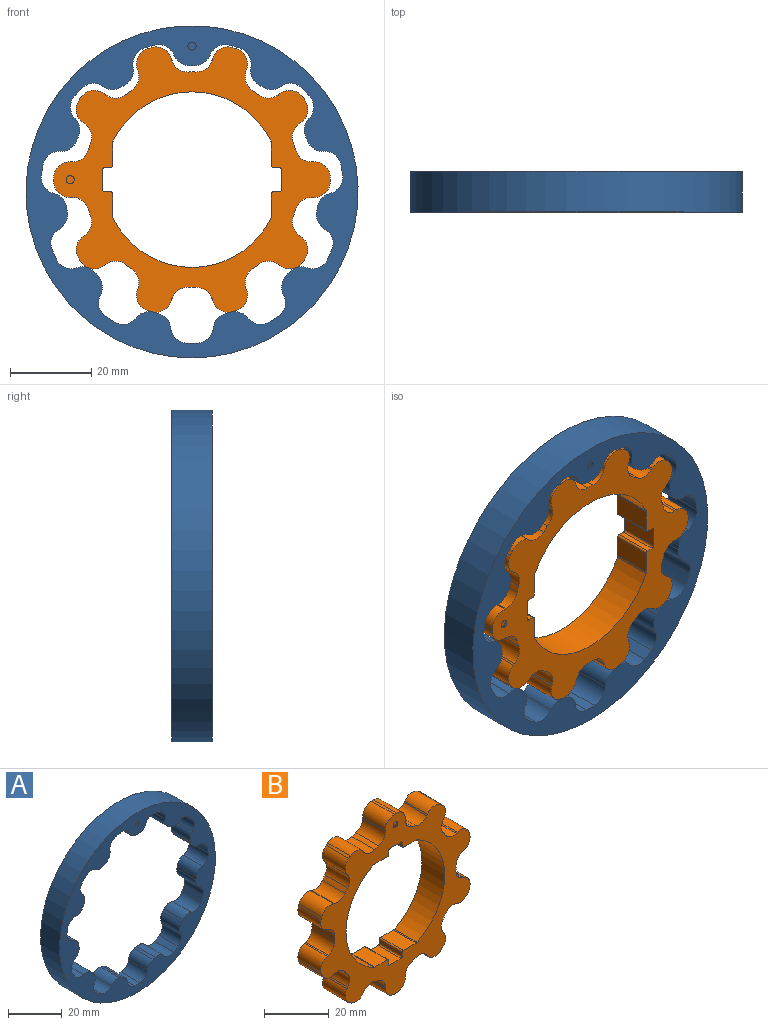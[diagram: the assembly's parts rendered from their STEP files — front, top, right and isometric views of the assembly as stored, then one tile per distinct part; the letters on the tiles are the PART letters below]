
ASSEMBLY  parts=2 mates=1
PART A: 71 faces, bbox 81.7x10x81.7 mm
  f0: cylinder r=31.07mm len=9.95mm, axis (0,1,0), area 12.2mm2, adj f11,f12,f18,f46
  f1: cylinder r=31.07mm len=9.95mm, axis (0,1,0), area 12.2mm2, adj f11,f12,f45,f48
  f2: cylinder r=31.07mm len=9.95mm, axis (0,1,0), area 12.2mm2, adj f11,f12,f42,f43
  f3: cylinder r=31.07mm len=9.95mm, axis (0,1,0), area 12.2mm2, adj f11,f12,f39,f40
  f4: cylinder r=31.07mm len=9.95mm, axis (0,1,0), area 12.2mm2, adj f11,f12,f36,f37
  f5: cylinder r=31.07mm len=9.95mm, axis (0,1,0), area 12.2mm2, adj f11,f12,f33,f34
  f6: cylinder r=31.07mm len=9.95mm, axis (0,1,0), area 12.2mm2, adj f11,f12,f30,f31
  f7: cylinder r=31.07mm len=9.95mm, axis (0,1,0), area 12.2mm2, adj f11,f12,f27,f28
  f8: cylinder r=31.07mm len=9.95mm, axis (0,1,0), area 12.2mm2, adj f11,f12,f24,f25
  f9: cylinder r=31.07mm len=9.95mm, axis (0,1,0), area 12.2mm2, adj f11,f12,f21,f22
  f10: cylinder r=31.07mm len=9.95mm, axis (0,1,0), area 12.2mm2, adj f11,f12,f17,f19
  f11: plane 81.72x81.72mm, normal (0,-1,0), area 1518mm2, adj f0,f1,f2,f3,f4,f5,f6,f7
  f12: plane 81.72x81.72mm, normal (0,1,0), area 1521.2mm2, adj f0,f1,f2,f3,f4,f5,f6,f7
  f13: cylinder r=40.86mm len=81.72mm, axis (0,1,0), area 2554.5mm2, adj f11,f12
  f14: cylinder r=1mm len=2mm, axis (0,-1,0), area 3.1mm2, adj f11,f15
  f15: plane 2x2mm, normal (0,-1,0), area 3.1mm2, adj f14
  f16: cylinder r=37.24mm len=9.95mm, axis (0,-1,0), area 27.6mm2, adj f11,f12,f69,f70
  f17: cylinder r=4mm len=9.95mm, axis (0,-1,0), area 48.8mm2, adj f10,f11,f12,f69
  f18: cylinder r=4mm len=9.95mm, axis (0,-1,0), area 48.8mm2, adj f0,f11,f12,f70
  f19: cylinder r=4mm len=9.95mm, axis (0,-1,0), area 48.8mm2, adj f10,f11,f12,f68
  f20: cylinder r=37.24mm len=9.95mm, axis (0,-1,0), area 27.6mm2, adj f11,f12,f67,f68
  f21: cylinder r=4mm len=9.95mm, axis (0,-1,0), area 48.8mm2, adj f9,f11,f12,f67
  f22: cylinder r=4mm len=9.95mm, axis (0,-1,0), area 48.8mm2, adj f9,f11,f12,f66
  f23: cylinder r=37.24mm len=9.95mm, axis (0,-1,0), area 27.6mm2, adj f11,f12,f65,f66
  f24: cylinder r=4mm len=9.95mm, axis (0,-1,0), area 48.8mm2, adj f8,f11,f12,f65
  f25: cylinder r=4mm len=9.95mm, axis (0,-1,0), area 48.8mm2, adj f8,f11,f12,f64
  f26: cylinder r=37.24mm len=9.95mm, axis (0,-1,0), area 27.6mm2, adj f11,f12,f63,f64
  f27: cylinder r=4mm len=9.95mm, axis (0,-1,0), area 48.8mm2, adj f7,f11,f12,f63
  f28: cylinder r=4mm len=9.95mm, axis (0,-1,0), area 48.8mm2, adj f7,f11,f12,f62
  f29: cylinder r=37.24mm len=9.95mm, axis (0,-1,0), area 27.6mm2, adj f11,f12,f61,f62
  f30: cylinder r=4mm len=9.95mm, axis (0,-1,0), area 48.8mm2, adj f6,f11,f12,f61
  f31: cylinder r=4mm len=9.95mm, axis (0,-1,0), area 48.8mm2, adj f6,f11,f12,f60
  f32: cylinder r=37.24mm len=9.95mm, axis (0,-1,0), area 27.6mm2, adj f11,f12,f59,f60
  f33: cylinder r=4mm len=9.95mm, axis (0,-1,0), area 48.8mm2, adj f5,f11,f12,f59
  f34: cylinder r=4mm len=9.95mm, axis (0,-1,0), area 48.8mm2, adj f5,f11,f12,f58
  f35: cylinder r=37.24mm len=9.95mm, axis (0,-1,0), area 27.6mm2, adj f11,f12,f57,f58
  f36: cylinder r=4mm len=9.95mm, axis (0,-1,0), area 48.8mm2, adj f4,f11,f12,f57
  f37: cylinder r=4mm len=9.95mm, axis (0,-1,0), area 48.8mm2, adj f4,f11,f12,f56
  f38: cylinder r=37.24mm len=9.95mm, axis (0,-1,0), area 27.6mm2, adj f11,f12,f55,f56
  f39: cylinder r=4mm len=9.95mm, axis (0,-1,0), area 48.8mm2, adj f3,f11,f12,f55
  f40: cylinder r=4mm len=9.95mm, axis (0,-1,0), area 48.8mm2, adj f3,f11,f12,f54
  f41: cylinder r=37.24mm len=9.95mm, axis (0,-1,0), area 27.6mm2, adj f11,f12,f53,f54
  f42: cylinder r=4mm len=9.95mm, axis (0,-1,0), area 48.8mm2, adj f2,f11,f12,f53
  f43: cylinder r=4mm len=9.95mm, axis (0,-1,0), area 48.8mm2, adj f2,f11,f12,f52
  f44: cylinder r=37.24mm len=9.95mm, axis (0,-1,0), area 27.6mm2, adj f11,f12,f51,f52
  f45: cylinder r=4mm len=9.95mm, axis (0,-1,0), area 48.8mm2, adj f1,f11,f12,f51
  f46: cylinder r=4mm len=9.95mm, axis (0,-1,0), area 48.8mm2, adj f0,f11,f12,f49
  f47: cylinder r=37.24mm len=9.95mm, axis (0,-1,0), area 27.6mm2, adj f11,f12,f49,f50
  f48: cylinder r=4mm len=9.95mm, axis (0,-1,0), area 48.8mm2, adj f1,f11,f12,f50
  f49: cylinder r=4mm len=9.95mm, axis (0,-1,0), area 57.9mm2, adj f11,f12,f46,f47
  f50: cylinder r=4mm len=9.95mm, axis (0,-1,0), area 57.9mm2, adj f11,f12,f47,f48
  f51: cylinder r=4mm len=9.95mm, axis (0,-1,0), area 57.9mm2, adj f11,f12,f44,f45
  f52: cylinder r=4mm len=9.95mm, axis (0,-1,0), area 57.9mm2, adj f11,f12,f43,f44
  f53: cylinder r=4mm len=9.95mm, axis (0,-1,0), area 57.9mm2, adj f11,f12,f41,f42
  f54: cylinder r=4mm len=9.95mm, axis (0,-1,0), area 57.9mm2, adj f11,f12,f40,f41
  f55: cylinder r=4mm len=9.95mm, axis (0,-1,0), area 57.9mm2, adj f11,f12,f38,f39
  f56: cylinder r=4mm len=9.95mm, axis (0,-1,0), area 57.9mm2, adj f11,f12,f37,f38
  f57: cylinder r=4mm len=9.95mm, axis (0,-1,0), area 57.9mm2, adj f11,f12,f35,f36
  f58: cylinder r=4mm len=9.95mm, axis (0,-1,0), area 57.9mm2, adj f11,f12,f34,f35
  f59: cylinder r=4mm len=9.95mm, axis (0,-1,0), area 57.9mm2, adj f11,f12,f32,f33
  f60: cylinder r=4mm len=9.95mm, axis (0,-1,0), area 57.9mm2, adj f11,f12,f31,f32
  f61: cylinder r=4mm len=9.95mm, axis (0,-1,0), area 57.9mm2, adj f11,f12,f29,f30
  f62: cylinder r=4mm len=9.95mm, axis (0,-1,0), area 57.9mm2, adj f11,f12,f28,f29
  f63: cylinder r=4mm len=9.95mm, axis (0,-1,0), area 57.9mm2, adj f11,f12,f26,f27
  f64: cylinder r=4mm len=9.95mm, axis (0,-1,0), area 57.9mm2, adj f11,f12,f25,f26
  f65: cylinder r=4mm len=9.95mm, axis (0,-1,0), area 57.9mm2, adj f11,f12,f23,f24
  f66: cylinder r=4mm len=9.95mm, axis (0,-1,0), area 57.9mm2, adj f11,f12,f22,f23
  f67: cylinder r=4mm len=9.95mm, axis (0,-1,0), area 57.9mm2, adj f11,f12,f20,f21
  f68: cylinder r=4mm len=9.95mm, axis (0,-1,0), area 57.9mm2, adj f11,f12,f19,f20
  f69: cylinder r=4mm len=9.95mm, axis (0,-1,0), area 57.9mm2, adj f11,f12,f16,f17
  f70: cylinder r=4mm len=9.95mm, axis (0,-1,0), area 57.9mm2, adj f11,f12,f16,f18
PART B: 108 faces, bbox 65.3x10x68 mm
  f0: cylinder r=34mm len=9.95mm, axis (0,1,0), area 9.4mm2, adj f9,f10,f41,f101
  f1: cylinder r=34mm len=9.95mm, axis (0,1,0), area 9.4mm2, adj f9,f10,f100,f107
  f2: cylinder r=34mm len=9.95mm, axis (0,1,0), area 9.4mm2, adj f9,f10,f93,f94
  f3: cylinder r=34mm len=9.95mm, axis (0,1,0), area 9.4mm2, adj f9,f10,f86,f87
  f4: cylinder r=34mm len=9.95mm, axis (0,1,0), area 9.4mm2, adj f9,f10,f79,f80
  f5: cylinder r=34mm len=9.95mm, axis (0,1,0), area 9.4mm2, adj f9,f10,f72,f73
  f6: cylinder r=34mm len=9.95mm, axis (0,1,0), area 9.4mm2, adj f9,f10,f65,f66
  f7: cylinder r=34mm len=9.95mm, axis (0,1,0), area 9.4mm2, adj f9,f10,f58,f59
  f8: cylinder r=34mm len=9.95mm, axis (0,1,0), area 9.4mm2, adj f9,f10,f51,f52
  f9: plane 68x65.32mm, normal (0,-1,0), area 1401.2mm2, adj f0,f1,f2,f3,f4,f5,f6,f7
  f10: plane 68x65.32mm, normal (0,1,0), area 1404.3mm2, adj f0,f1,f2,f3,f4,f5,f6,f7
  f11: cylinder r=1mm len=9.95mm, axis (0,1,0), area 4.5mm2, adj f9,f10,f12,f34
  f12: plane 9.95x5.56mm, normal (0,0,-1), area 55.3mm2, adj f9,f10,f11,f13
  f13: cylinder r=0.5mm len=9.95mm, axis (0,1,0), area 7.8mm2, adj f9,f10,f12,f14
  f14: plane 9.95x1.5mm, normal (1,0,0), area 14.9mm2, adj f9,f10,f13,f15
  f15: cylinder r=0.5mm len=9.95mm, axis (0,1,0), area 7.8mm2, adj f9,f10,f14,f16
  f16: plane 9.95x5mm, normal (0,0,-1), area 49.8mm2, adj f9,f10,f15,f17
  f17: cylinder r=0.5mm len=9.95mm, axis (0,1,0), area 7.8mm2, adj f9,f10,f16,f18
  f18: plane 9.95x1.5mm, normal (-1,0,0), area 14.9mm2, adj f9,f10,f17,f19
  f19: cylinder r=0.5mm len=9.95mm, axis (0,1,0), area 7.8mm2, adj f9,f10,f18,f20
  f20: plane 9.95x5.56mm, normal (0,0,-1), area 55.3mm2, adj f9,f10,f19,f21
  f21: cylinder r=1mm len=9.95mm, axis (0,1,0), area 4.5mm2, adj f9,f10,f20,f22
  f22: cylinder r=21.6mm len=38.8mm, axis (0,1,0), area 479.4mm2, adj f9,f10,f21,f23
  f23: cylinder r=1mm len=9.95mm, axis (0,1,0), area 4.5mm2, adj f9,f10,f22,f24
  f24: plane 9.95x5.56mm, normal (0,0,1), area 55.3mm2, adj f9,f10,f23,f25
  f25: cylinder r=0.5mm len=9.95mm, axis (0,1,0), area 7.8mm2, adj f9,f10,f24,f26
  f26: plane 9.95x1.5mm, normal (-1,0,0), area 14.9mm2, adj f9,f10,f25,f27
  f27: cylinder r=0.5mm len=9.95mm, axis (0,1,0), area 7.8mm2, adj f9,f10,f26,f28
  f28: plane 9.95x5mm, normal (0,0,1), area 49.8mm2, adj f9,f10,f27,f29
  f29: cylinder r=0.5mm len=9.95mm, axis (0,1,0), area 7.8mm2, adj f9,f10,f28,f30
  f30: plane 9.95x1.5mm, normal (1,0,0), area 14.9mm2, adj f9,f10,f29,f31
  f31: cylinder r=0.5mm len=9.95mm, axis (0,1,0), area 7.8mm2, adj f9,f10,f30,f32
  f32: plane 9.95x5.56mm, normal (0,0,1), area 55.3mm2, adj f9,f10,f31,f33
  f33: cylinder r=1mm len=9.95mm, axis (0,1,0), area 4.5mm2, adj f9,f10,f32,f34
  f34: cylinder r=21.6mm len=38.8mm, axis (0,1,0), area 479.4mm2, adj f9,f10,f11,f33
  f35: cylinder r=34mm len=9.95mm, axis (0,1,0), area 9.4mm2, adj f9,f10,f40,f45
  f36: cylinder r=1mm len=2mm, axis (0,-1,0), area 3.1mm2, adj f9,f37
  f37: plane 2x2mm, normal (0,-1,0), area 3.1mm2, adj f36
  f38: cylinder r=4mm len=9.95mm, axis (0,-1,0), area 57.3mm2, adj f9,f10,f39,f44
  f39: plane 9.95x0.5mm, normal (-0.17,0,0.99), area 5mm2, adj f9,f10,f38,f40
  f40: cylinder r=4mm len=9.95mm, axis (0,-1,0), area 67.8mm2, adj f9,f10,f35,f39
  f41: cylinder r=4mm len=9.95mm, axis (0,-1,0), area 67.8mm2, adj f0,f9,f10,f42
  f42: plane 9.95x0.5mm, normal (-0.17,0,-0.99), area 5mm2, adj f9,f10,f41,f43
  f43: cylinder r=4mm len=9.95mm, axis (0,-1,0), area 57.3mm2, adj f9,f10,f42,f44
  f44: cylinder r=26.5mm len=9.95mm, axis (0,-1,0), area 18.5mm2, adj f9,f10,f38,f43
  f45: cylinder r=4mm len=9.95mm, axis (0,-1,0), area 67.8mm2, adj f9,f10,f35,f46
  f46: plane 9.95x0.45mm, normal (0.45,0,-0.9), area 5mm2, adj f9,f10,f45,f47
  f47: cylinder r=4mm len=9.95mm, axis (0,-1,0), area 57.3mm2, adj f9,f10,f46,f48
  f48: cylinder r=26.5mm len=9.95mm, axis (0,-1,0), area 18.5mm2, adj f9,f10,f47,f49
  f49: cylinder r=4mm len=9.95mm, axis (0,-1,0), area 57.3mm2, adj f9,f10,f48,f50
  f50: plane 9.95x0.36mm, normal (-0.71,0,0.7), area 5mm2, adj f9,f10,f49,f51
  f51: cylinder r=4mm len=9.95mm, axis (0,-1,0), area 67.8mm2, adj f8,f9,f10,f50
  f52: cylinder r=4mm len=9.95mm, axis (0,-1,0), area 67.8mm2, adj f8,f9,f10,f53
  f53: plane 9.95x0.45mm, normal (0.89,0,-0.46), area 5mm2, adj f9,f10,f52,f54
  f54: cylinder r=4mm len=9.95mm, axis (0,-1,0), area 57.3mm2, adj f9,f10,f53,f55
  f55: cylinder r=26.5mm len=9.95mm, axis (0,-1,0), area 18.5mm2, adj f9,f10,f54,f56
  f56: cylinder r=4mm len=9.95mm, axis (0,-1,0), area 57.3mm2, adj f9,f10,f55,f57
  f57: plane 9.95x0.5mm, normal (-0.99,0,0.15), area 5mm2, adj f9,f10,f56,f58
  f58: cylinder r=4mm len=9.95mm, axis (0,-1,0), area 67.8mm2, adj f7,f9,f10,f57
  f59: cylinder r=4mm len=9.95mm, axis (0,-1,0), area 67.8mm2, adj f7,f9,f10,f60
  f60: plane 9.95x0.5mm, normal (0.99,0,0.15), area 5mm2, adj f9,f10,f59,f61
  f61: cylinder r=4mm len=9.95mm, axis (0,-1,0), area 57.3mm2, adj f9,f10,f60,f62
  f62: cylinder r=26.5mm len=9.95mm, axis (0,-1,0), area 18.5mm2, adj f9,f10,f61,f63
  f63: cylinder r=4mm len=9.95mm, axis (0,-1,0), area 57.3mm2, adj f9,f10,f62,f64
  f64: plane 9.95x0.45mm, normal (-0.89,0,-0.46), area 5mm2, adj f9,f10,f63,f65
  f65: cylinder r=4mm len=9.95mm, axis (0,-1,0), area 67.8mm2, adj f6,f9,f10,f64
  f66: cylinder r=4mm len=9.95mm, axis (0,-1,0), area 67.8mm2, adj f6,f9,f10,f67
  f67: plane 9.95x0.36mm, normal (0.71,0,0.7), area 5mm2, adj f9,f10,f66,f68
  f68: cylinder r=4mm len=9.95mm, axis (0,-1,0), area 57.3mm2, adj f9,f10,f67,f69
  f69: cylinder r=26.5mm len=9.95mm, axis (0,-1,0), area 18.5mm2, adj f9,f10,f68,f70
  f70: cylinder r=4mm len=9.95mm, axis (0,-1,0), area 57.3mm2, adj f9,f10,f69,f71
  f71: plane 9.95x0.45mm, normal (-0.45,0,-0.9), area 5mm2, adj f9,f10,f70,f72
  f72: cylinder r=4mm len=9.95mm, axis (0,-1,0), area 67.8mm2, adj f5,f9,f10,f71
  f73: cylinder r=4mm len=9.95mm, axis (0,-1,0), area 67.8mm2, adj f5,f9,f10,f74
  f74: plane 9.95x0.5mm, normal (0.17,0,0.99), area 5mm2, adj f9,f10,f73,f75
  f75: cylinder r=4mm len=9.95mm, axis (0,-1,0), area 57.3mm2, adj f9,f10,f74,f76
  f76: cylinder r=26.5mm len=9.95mm, axis (0,-1,0), area 18.5mm2, adj f9,f10,f75,f77
  f77: cylinder r=4mm len=9.95mm, axis (0,-1,0), area 57.3mm2, adj f9,f10,f76,f78
  f78: plane 9.95x0.5mm, normal (0.17,0,-0.99), area 5mm2, adj f9,f10,f77,f79
  f79: cylinder r=4mm len=9.95mm, axis (0,-1,0), area 67.8mm2, adj f4,f9,f10,f78
  f80: cylinder r=4mm len=9.95mm, axis (0,-1,0), area 67.8mm2, adj f4,f9,f10,f81
  f81: plane 9.95x0.45mm, normal (-0.45,0,0.9), area 5mm2, adj f9,f10,f80,f82
  f82: cylinder r=4mm len=9.95mm, axis (0,-1,0), area 57.3mm2, adj f9,f10,f81,f83
  f83: cylinder r=26.5mm len=9.95mm, axis (0,-1,0), area 18.5mm2, adj f9,f10,f82,f84
  f84: cylinder r=4mm len=9.95mm, axis (0,-1,0), area 57.3mm2, adj f9,f10,f83,f85
  f85: plane 9.95x0.36mm, normal (0.71,0,-0.7), area 5mm2, adj f9,f10,f84,f86
  f86: cylinder r=4mm len=9.95mm, axis (0,-1,0), area 67.8mm2, adj f3,f9,f10,f85
  f87: cylinder r=4mm len=9.95mm, axis (0,-1,0), area 67.8mm2, adj f3,f9,f10,f88
  f88: plane 9.95x0.45mm, normal (-0.89,0,0.46), area 5mm2, adj f9,f10,f87,f89
  f89: cylinder r=4mm len=9.95mm, axis (0,-1,0), area 57.3mm2, adj f9,f10,f88,f90
  f90: cylinder r=26.5mm len=9.95mm, axis (0,-1,0), area 18.5mm2, adj f9,f10,f89,f91
  f91: cylinder r=4mm len=9.95mm, axis (0,-1,0), area 57.3mm2, adj f9,f10,f90,f92
  f92: plane 9.95x0.5mm, normal (0.99,0,-0.15), area 5mm2, adj f9,f10,f91,f93
  f93: cylinder r=4mm len=9.95mm, axis (0,-1,0), area 67.8mm2, adj f2,f9,f10,f92
  f94: cylinder r=4mm len=9.95mm, axis (0,-1,0), area 67.8mm2, adj f2,f9,f10,f95
  f95: plane 9.95x0.5mm, normal (-0.99,0,-0.15), area 5mm2, adj f9,f10,f94,f96
  f96: cylinder r=4mm len=9.95mm, axis (0,-1,0), area 57.3mm2, adj f9,f10,f95,f97
  f97: cylinder r=26.5mm len=9.95mm, axis (0,-1,0), area 18.5mm2, adj f9,f10,f96,f98
  f98: cylinder r=4mm len=9.95mm, axis (0,-1,0), area 57.3mm2, adj f9,f10,f97,f99
  f99: plane 9.95x0.45mm, normal (0.89,0,0.46), area 5mm2, adj f9,f10,f98,f100
  f100: cylinder r=4mm len=9.95mm, axis (0,-1,0), area 67.8mm2, adj f1,f9,f10,f99
  f101: cylinder r=4mm len=9.95mm, axis (0,-1,0), area 67.8mm2, adj f0,f9,f10,f102
  f102: plane 9.95x0.45mm, normal (0.45,0,0.9), area 5mm2, adj f9,f10,f101,f103
  f103: cylinder r=4mm len=9.95mm, axis (0,-1,0), area 57.3mm2, adj f9,f10,f102,f104
  f104: cylinder r=26.5mm len=9.95mm, axis (0,-1,0), area 18.5mm2, adj f9,f10,f103,f105
  f105: cylinder r=4mm len=9.95mm, axis (0,-1,0), area 57.3mm2, adj f9,f10,f104,f106
  f106: plane 9.95x0.36mm, normal (-0.71,0,-0.7), area 5mm2, adj f9,f10,f105,f107
  f107: cylinder r=4mm len=9.95mm, axis (0,-1,0), area 67.8mm2, adj f1,f9,f10,f106
PLACE A t=(1.11,-0.04,-0.98)mm
PLACE B rot(axis=(0,-1,0),90deg) t=(1.11,-0.04,2.02)mm
MATE fastened B.f22 <-> A.f11  axis (0,1,0) through (1.11,-5.01,2.02)mm
